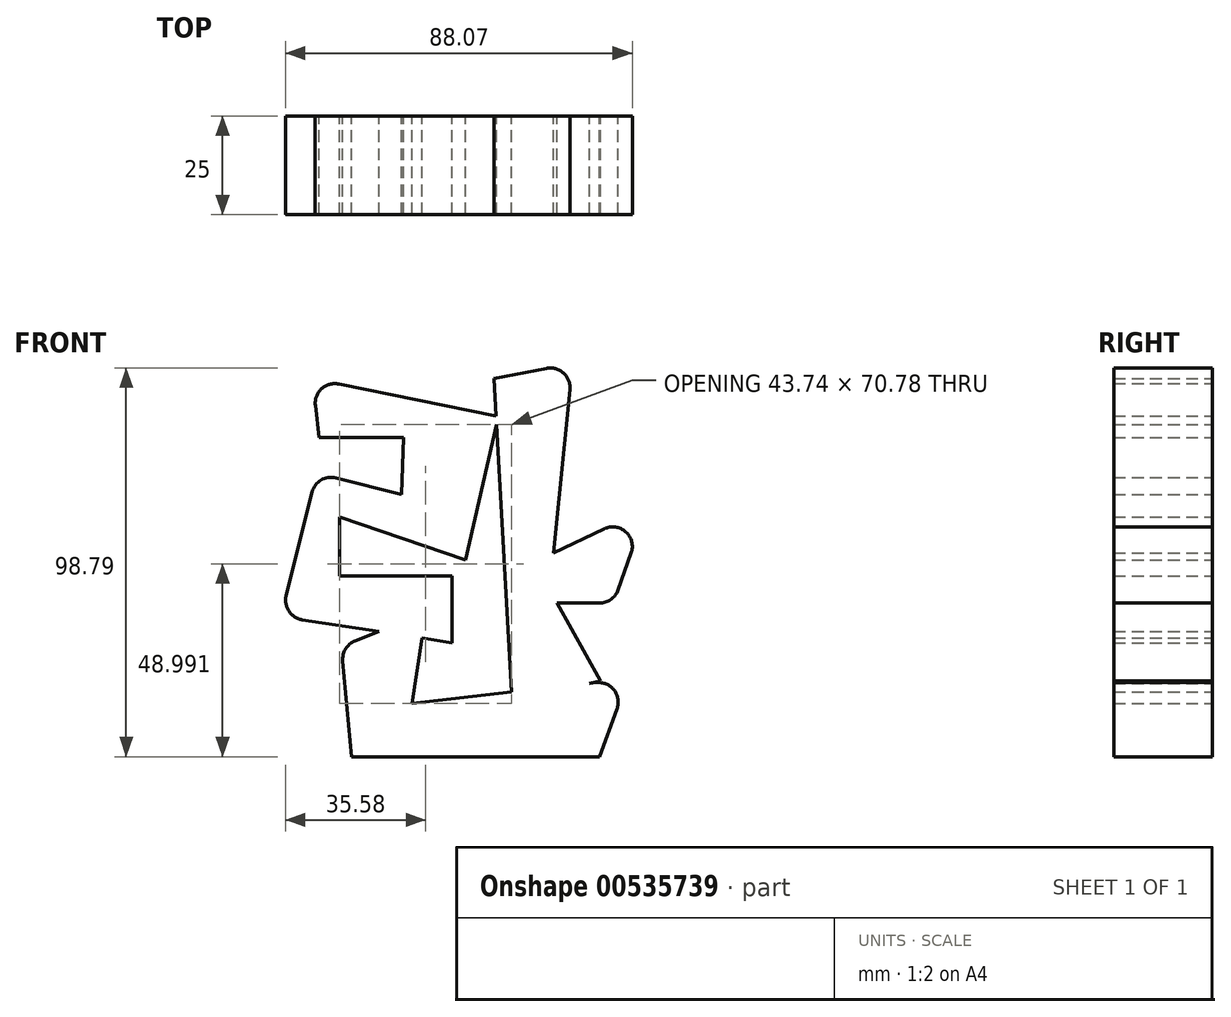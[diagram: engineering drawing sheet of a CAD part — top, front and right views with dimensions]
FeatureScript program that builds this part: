
annotation { "Feature Type Name" : "Feature", "Feature Type Description" : "" }
export const myFeature = defineFeature(function(context is Context, id is Id, definition is map)
    precondition{}
    {
        {
            var Q0;
            Q0=qCreatedBy(makeId("Front.planeOp"),FACE);
            var sketch = newSketch(context, id + "F0", { "sketchPlane" : qUnion([Q0])});
            skLineSegment(sketch, "E0", {"start": v(-28.7, 33.73) * mm, "end": v(11.85, 25.45) * mm});
            skLineSegment(sketch, "E1", {"start": v(11.85, 25.45) * mm, "end": v(3.51, -10.97) * mm});
            skLineSegment(sketch, "E2", {"start": v(3.51, -10.97) * mm, "end": v(-28.52, 0) * mm});
            skLineSegment(sketch, "E3", {"start": v(-28.52, 0) * mm, "end": v(-28.52, -15.01) * mm});
            skLineSegment(sketch, "E4", {"start": v(-28.52, -15.01) * mm, "end": v(0, -15.01) * mm});
            skLineSegment(sketch, "E5", {"start": v(0, -15.01) * mm, "end": v(0, -32) * mm});
            skLineSegment(sketch, "E6", {"start": v(0, -32) * mm, "end": v(-38, -26.16) * mm});
            skLineSegment(sketch, "E7", {"start": v(-42.08, -20.01) * mm, "end": v(-35.52, 6.25) * mm});
            skLineSegment(sketch, "E8", {"start": v(-29.45, 9.89) * mm, "end": v(-12.73, 5.7) * mm});
            skLineSegment(sketch, "E9", {"start": v(-12.73, 5.7) * mm, "end": v(-12.21, 20.18) * mm});
            skLineSegment(sketch, "E10", {"start": v(-12.21, 20.18) * mm, "end": v(-33.79, 20.18) * mm});
            skLineSegment(sketch, "E11", {"start": v(-33.79, 20.18) * mm, "end": v(-34.68, 28.29) * mm});
            skLineSegment(sketch, "E12", {"start": v(10.71, 35.1) * mm, "end": v(15.36, -46.95) * mm});
            skLineSegment(sketch, "E13", {"start": v(15.36, -46.95) * mm, "end": v(37.74, -41.69) * mm});
            skLineSegment(sketch, "E14", {"start": v(37.74, -41.69) * mm, "end": v(26.77, -21.94) * mm});
            skLineSegment(sketch, "E15", {"start": v(26.77, -21.94) * mm, "end": v(37.53, -21.94) * mm});
            skLineSegment(sketch, "E16", {"start": v(42.24, -18.6) * mm, "end": v(45.55, -9.23) * mm});
            skLineSegment(sketch, "E17", {"start": v(38.67, -3.06) * mm, "end": v(25.89, -9.21) * mm});
            skLineSegment(sketch, "E18", {"start": v(25.89, -9.21) * mm, "end": v(30, 32.3) * mm});
            skLineSegment(sketch, "E19", {"start": v(24.06, 37.7) * mm, "end": v(10.71, 35.1) * mm});
            skLineSegment(sketch, "E20", {"start": v(-27.73, -36.66) * mm, "end": v(-25.45, -61) * mm});
            skLineSegment(sketch, "E21", {"start": v(-25.45, -61) * mm, "end": v(37.48, -61) * mm});
            skLineSegment(sketch, "E22", {"start": v(37.48, -61) * mm, "end": v(41.96, -48.85) * mm});
            skLineSegment(sketch, "E23", {"start": v(36.7, -42.15) * mm, "end": v(-10.1, -47.4) * mm});
            skLineSegment(sketch, "E24", {"start": v(-10.1, -47.4) * mm, "end": v(-6.56, -24.46) * mm});
            skLineSegment(sketch, "E25", {"start": v(-6.56, -24.46) * mm, "end": v(-24.58, -31.54) * mm});
            skPoint(sketch, "E26.visualSharp", {"position": v(-35.43, 35.1) * mm});
            skArc(sketch, "E26.filletArc", {"start": v(-28.7, 33.73) * mm, "mid": v(-33.08, 32.53) * mm, "end": v(-34.68, 28.29) * mm});
            skPoint(sketch, "E27.visualSharp", {"position": v(30.65, 39) * mm});
            skArc(sketch, "E27.filletArc", {"start": v(30, 32.3) * mm, "mid": v(28.38, 36.5) * mm, "end": v(24.06, 37.7) * mm});
            skPoint(sketch, "E28.visualSharp", {"position": v(-43.41, -25.33) * mm});
            skArc(sketch, "E28.filletArc", {"start": v(-42.08, -20.01) * mm, "mid": v(-41.4, -24) * mm, "end": v(-38, -26.16) * mm});
            skPoint(sketch, "E29.visualSharp", {"position": v(49.58, 2.2) * mm});
            skArc(sketch, "E29.filletArc", {"start": v(45.55, -9.23) * mm, "mid": v(44.17, -3.84) * mm, "end": v(38.67, -3.06) * mm});
            skPoint(sketch, "E30.visualSharp", {"position": v(-28.08, -32.91) * mm});
            skArc(sketch, "E30.filletArc", {"start": v(-24.58, -31.54) * mm, "mid": v(-27.01, -33.57) * mm, "end": v(-27.73, -36.66) * mm});
            skPoint(sketch, "E31.visualSharp", {"position": v(44.76, -41.25) * mm});
            skArc(sketch, "E31.filletArc", {"start": v(41.96, -48.85) * mm, "mid": v(41.2, -44.03) * mm, "end": v(36.7, -42.15) * mm});
            skPoint(sketch, "E32.visualSharp", {"position": v(-34.3, 11.1) * mm});
            skArc(sketch, "E32.filletArc", {"start": v(-29.45, 9.89) * mm, "mid": v(-33.24, 9.32) * mm, "end": v(-35.52, 6.25) * mm});
            skPoint(sketch, "E33.visualSharp", {"position": v(41.07, -21.94) * mm});
            skArc(sketch, "E33.filletArc", {"start": v(37.53, -21.94) * mm, "mid": v(40.42, -21.02) * mm, "end": v(42.24, -18.6) * mm});
            skSolve(sketch);
        }
        {
            var Q0;
            {var subQ12=sQuery(id+"F0.wireOp",EDGE,"E2");Q0=makeQuery(id+"F0.imprint","IMPRINT",FACE,{"disambiguationData":[TD([[makeQuery(id+"F0.imprint","IMPRINT",EDGE,{"derivedFrom":subQ12}),-1.0]])]});}
            var Q1;
            {var subQ0=sQuery(id+"F0.wireOp",EDGE,"E25");var subQ1=sQuery(id+"F0.wireOp",EDGE,"E6");var subQ2=makeQuery(id+"F0.imprint","INTERSECT",VERTEX,{"derivedFrom":[subQ1,subQ0]});Q1=makeQuery(id+"F0.imprint","IMPRINT",FACE,{"disambiguationData":[TD([[makeQuery(id+"F0.imprint","IMPRINT",EDGE,{"disambiguationData":[TD([[subQ2,1.0]])],"derivedFrom":subQ1}),-1.0]])]});}
            var Q2;
            Q2=makeQuery(id+"F0.imprint","IMPRINT",FACE,{"disambiguationData":[TD([[makeQuery(id+"F0.imprint","IMPRINT",EDGE,{"derivedFrom":sQuery(id+"F0.wireOp",EDGE,"E20")}),1.0]])]});
            var Q3;
            {var subQ0=sQuery(id+"F0.wireOp",EDGE,"E13");var subQ1=sQuery(id+"F0.wireOp",EDGE,"E12");var subQ2=makeQuery(id+"F0.imprint","INTERSECT",VERTEX,{"derivedFrom":[subQ1,subQ0]});Q3=makeQuery(id+"F0.imprint","IMPRINT",FACE,{"disambiguationData":[TD([[makeQuery(id+"F0.imprint","IMPRINT",EDGE,{"disambiguationData":[TD([[subQ2,1.0]])],"derivedFrom":subQ1}),1.0]])]});}
            var Q4;
            {var subQ5=sQuery(id+"F0.wireOp",EDGE,"E14");Q4=makeQuery(id+"F0.imprint","IMPRINT",FACE,{"disambiguationData":[TD([[makeQuery(id+"F0.imprint","IMPRINT",EDGE,{"derivedFrom":subQ5}),1.0]])]});}
            var Q5;
            {var subQ0=sQuery(id+"F0.wireOp",EDGE,"E1");var subQ1=sQuery(id+"F0.wireOp",EDGE,"E0");var subQ2=makeQuery(id+"F0.imprint","INTERSECT",VERTEX,{"derivedFrom":[subQ1,subQ0]});Q5=makeQuery(id+"F0.imprint","IMPRINT",FACE,{"disambiguationData":[TD([[makeQuery(id+"F0.imprint","IMPRINT",EDGE,{"disambiguationData":[TD([[subQ2,1.0]])],"derivedFrom":subQ1}),-1.0]])]});}
            extrude(context, id + "F1", {"entities" : qUnion([Q0, Q1, Q2, Q3, Q4, Q5]), "depth" : 25 * mm, "offsetDistance" : 25 * mm});
        }
    });
